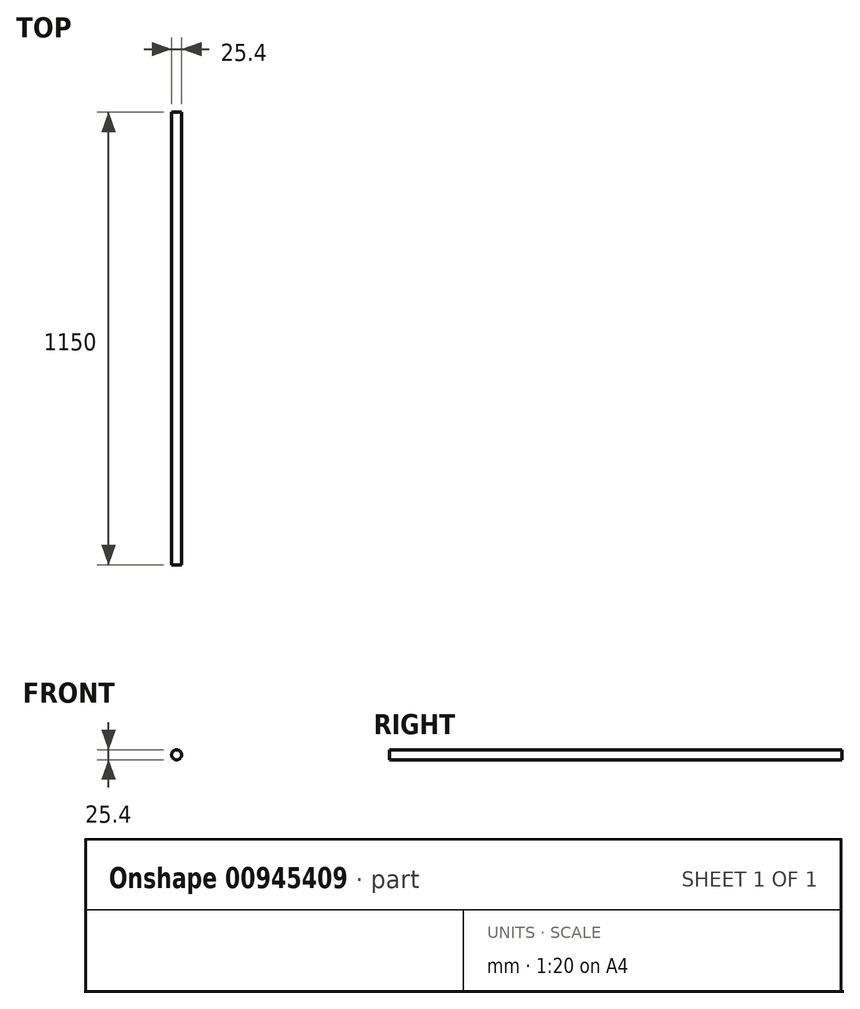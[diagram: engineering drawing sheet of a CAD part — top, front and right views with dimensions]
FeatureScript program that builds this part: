
annotation { "Feature Type Name" : "Feature", "Feature Type Description" : "" }
export const myFeature = defineFeature(function(context is Context, id is Id, definition is map)
    precondition{}
    {
        {
            var Q0;
            Q0=qCreatedBy(makeId("Front.planeOp"),FACE);
            var sketch = newSketch(context, id + "F0", { "sketchPlane" : qUnion([Q0])});
            skCircle(sketch, "E0", {"center": v(0, 0) * mm, "radius": 12.7 * mm});
            skSolve(sketch);
        }
        {
            var Q0;
            Q0=sQuery(id+"F0.wireOp",EDGE,"E0");
            extrude(context, id + "F1", {"bodyType" : ToolBodyType.SURFACE, "surfaceEntities" : qUnion([Q0]), "depth" : 1150 * mm, "offsetDistance" : 25.4 * mm});
        }
    });
